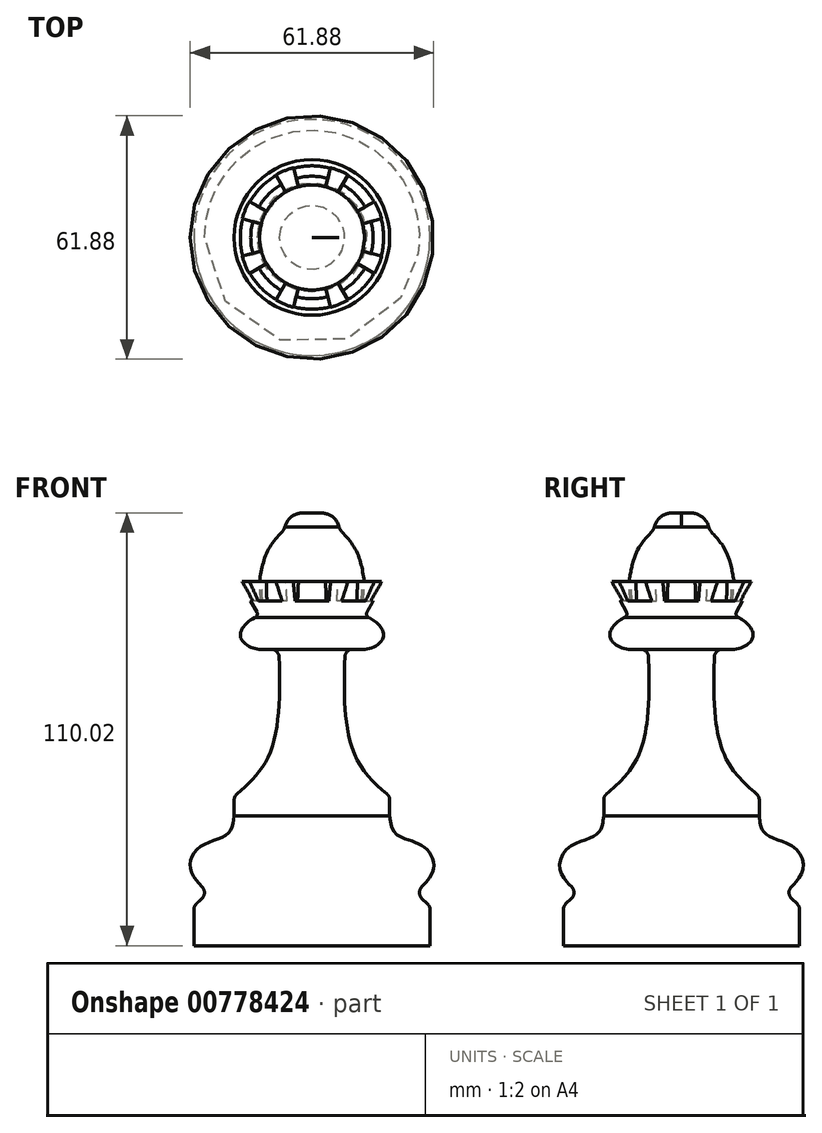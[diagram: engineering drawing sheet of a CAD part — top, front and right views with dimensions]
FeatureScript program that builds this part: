
annotation { "Feature Type Name" : "Feature", "Feature Type Description" : "" }
export const myFeature = defineFeature(function(context is Context, id is Id, definition is map)
    precondition{}
    {
        {
            var Q0;
            Q0=qCreatedBy(makeId("Front.planeOp"),FACE);
            var sketch = newSketch(context, id + "F0", { "sketchPlane" : qUnion([Q0])});
            skLineSegment(sketch, "E0", {"start": v(0, 0) * mm, "end": v(30, 0) * mm});
            skLineSegment(sketch, "E1", {"start": v(30, 0) * mm, "end": v(30, 10) * mm});
            skLineSegment(sketch, "E2", {"start": v(30, 10) * mm, "end": v(26.46, 13.53) * mm});
            skPoint(sketch, "E3.2.internal.snap0", {"position": v(28.23, 11.77) * mm});
            skFitSpline(sketch, "E3", {"points": [v(26.46, 13.53) * mm, v(30.89, 19.7) * mm, v(28.23, 25.27) * mm, v(21.35, 28.45) * mm, v(19.76, 32.96) * mm], "startDerivative": vector(22.56, 21.82) * mm, "endDerivative": vector(-2.53, 23.93) * mm});
            skLineSegment(sketch, "E4", {"start": v(19.76, 32.96) * mm, "end": v(19.76, 37.96) * mm});
            skFitSpline(sketch, "E5", {"points": [v(19.76, 37.96) * mm, v(10.75, 48.85) * mm, v(8.46, 75.35) * mm], "startDerivative": vector(-25.28, 21.61) * mm, "endDerivative": vector(2.63, 51.62) * mm});
            skLineSegment(sketch, "E6", {"start": v(8.46, 75.35) * mm, "end": v(13.46, 75.35) * mm});
            skFitSpline(sketch, "E7", {"points": [v(13.46, 75.35) * mm, v(18.17, 78.53) * mm, v(13.46, 83.83) * mm], "startDerivative": vector(11.88, 0.45) * mm, "endDerivative": vector(-15.94, 5.75) * mm});
            skLineSegment(sketch, "E8", {"start": v(13.46, 83.83) * mm, "end": v(18.34, 92.56) * mm});
            skLineSegment(sketch, "E9", {"start": v(18.34, 92.56) * mm, "end": v(13.34, 92.56) * mm});
            skLineSegment(sketch, "E10", {"start": v(0, 0) * mm, "end": v(0, 110) * mm});
            skFitSpline(sketch, "E11", {"points": [v(13.34, 92.56) * mm, v(11.31, 100.2) * mm, v(7.05, 105.75) * mm], "startDerivative": vector(-2.67, 15.7) * mm, "endDerivative": vector(-9.98, 10.62) * mm});
            skFitSpline(sketch, "E12", {"points": [v(7.05, 105.75) * mm, v(4.34, 109.53) * mm, v(0, 110) * mm], "startDerivative": vector(-2.1, 13) * mm, "endDerivative": vector(-12.92, -0.33) * mm});
            skSolve(sketch);
        }
        {
            var Q0;
            Q0 = qSketchRegion(id + "F0", true);
            var Q1;
            Q1=sQuery(id+"F0.wireOp",EDGE,"E10");
            revolve(context, id + "F1", {"surfaceOperationType" : NewSurfaceOperationType.NEW, "entities" : qUnion([Q0]), "axis" : qUnion([Q1]), "revolveType" : RevolveType.FULL});
        }
        {
            var Q0;
            Q0=makeQuery(id+"F1.opRevolve","SWEPT_FACE",FACE,{"disambiguationData":[OSD([sQuery(id+"F0.wireOp",EDGE,"E9")])]});
            var sketch = newSketch(context, id + "F2", { "sketchPlane" : qUnion([Q0])});
            skArc(sketch, "E13", {"start": v(3.36, 12.53) * mm, "mid": v(0, 12.97) * mm, "end": v(-3.36, 12.53) * mm});
            skArc(sketch, "E14", {"start": v(5.12, 19.11) * mm, "mid": v(0, 19.79) * mm, "end": v(-5.12, 19.11) * mm});
            skLineSegment(sketch, "E15", {"start": v(3.36, 12.53) * mm, "end": v(5.12, 19.11) * mm});
            skLineSegment(sketch, "E16", {"start": v(-3.36, 12.53) * mm, "end": v(-5.12, 19.11) * mm});
            skLineSegment(sketch, "E17.1.0", {"start": v(-6.49, 11.23) * mm, "end": v(-9.9, 17.13) * mm});
            skArc(sketch, "E17.1.1", {"start": v(-9.9, 17.13) * mm, "mid": v(-14, 14) * mm, "end": v(-17.13, 9.9) * mm});
            skLineSegment(sketch, "E17.1.2", {"start": v(-11.23, 6.49) * mm, "end": v(-17.13, 9.9) * mm});
            skArc(sketch, "E17.1.3", {"start": v(-6.49, 11.23) * mm, "mid": v(-9.17, 9.17) * mm, "end": v(-11.23, 6.49) * mm});
            skLineSegment(sketch, "E17.2.0", {"start": v(-12.53, 3.36) * mm, "end": v(-19.11, 5.12) * mm});
            skArc(sketch, "E17.2.1", {"start": v(-19.11, 5.12) * mm, "mid": v(-19.79, 0) * mm, "end": v(-19.11, -5.12) * mm});
            skLineSegment(sketch, "E17.2.2", {"start": v(-12.53, -3.36) * mm, "end": v(-19.11, -5.12) * mm});
            skArc(sketch, "E17.2.3", {"start": v(-12.53, 3.36) * mm, "mid": v(-12.97, 0) * mm, "end": v(-12.53, -3.36) * mm});
            skLineSegment(sketch, "E17.3.0", {"start": v(-11.23, -6.49) * mm, "end": v(-17.13, -9.9) * mm});
            skArc(sketch, "E17.3.1", {"start": v(-17.13, -9.9) * mm, "mid": v(-14, -14) * mm, "end": v(-9.9, -17.13) * mm});
            skLineSegment(sketch, "E17.3.2", {"start": v(-6.49, -11.23) * mm, "end": v(-9.9, -17.13) * mm});
            skArc(sketch, "E17.3.3", {"start": v(-11.23, -6.49) * mm, "mid": v(-9.17, -9.17) * mm, "end": v(-6.49, -11.23) * mm});
            skLineSegment(sketch, "E17.4.0", {"start": v(-3.36, -12.53) * mm, "end": v(-5.12, -19.11) * mm});
            skArc(sketch, "E17.4.1", {"start": v(-5.12, -19.11) * mm, "mid": v(0, -19.79) * mm, "end": v(5.12, -19.11) * mm});
            skLineSegment(sketch, "E17.4.2", {"start": v(3.36, -12.53) * mm, "end": v(5.12, -19.11) * mm});
            skArc(sketch, "E17.4.3", {"start": v(-3.36, -12.53) * mm, "mid": v(0, -12.97) * mm, "end": v(3.36, -12.53) * mm});
            skLineSegment(sketch, "E17.5.0", {"start": v(6.49, -11.23) * mm, "end": v(9.9, -17.13) * mm});
            skArc(sketch, "E17.5.1", {"start": v(9.9, -17.13) * mm, "mid": v(14, -14) * mm, "end": v(17.13, -9.9) * mm});
            skLineSegment(sketch, "E17.5.2", {"start": v(11.23, -6.49) * mm, "end": v(17.13, -9.9) * mm});
            skArc(sketch, "E17.5.3", {"start": v(6.49, -11.23) * mm, "mid": v(9.17, -9.17) * mm, "end": v(11.23, -6.49) * mm});
            skLineSegment(sketch, "E17.6.0", {"start": v(12.53, -3.36) * mm, "end": v(19.11, -5.12) * mm});
            skArc(sketch, "E17.6.1", {"start": v(19.11, -5.12) * mm, "mid": v(19.79, 0) * mm, "end": v(19.11, 5.12) * mm});
            skLineSegment(sketch, "E17.6.2", {"start": v(12.53, 3.36) * mm, "end": v(19.11, 5.12) * mm});
            skArc(sketch, "E17.6.3", {"start": v(12.53, -3.36) * mm, "mid": v(12.97, 0) * mm, "end": v(12.53, 3.36) * mm});
            skLineSegment(sketch, "E17.7.0", {"start": v(11.23, 6.49) * mm, "end": v(17.13, 9.9) * mm});
            skArc(sketch, "E17.7.1", {"start": v(17.13, 9.9) * mm, "mid": v(14, 14) * mm, "end": v(9.9, 17.13) * mm});
            skLineSegment(sketch, "E17.7.2", {"start": v(6.49, 11.23) * mm, "end": v(9.9, 17.13) * mm});
            skArc(sketch, "E17.7.3", {"start": v(11.23, 6.49) * mm, "mid": v(9.17, 9.17) * mm, "end": v(6.49, 11.23) * mm});
            skSolve(sketch);
        }
        {
            var Q0;
            {var subQ0=sQuery(id+"F2.wireOp",EDGE,"E17.2.1");Q0=makeQuery(id+"F2.imprint","IMPRINT",FACE,{"disambiguationData":[TD([[makeQuery(id+"F2.imprint","IMPRINT",EDGE,{"derivedFrom":subQ0}),1.0]])]});}
            var Q1;
            {var subQ0=sQuery(id+"F2.wireOp",EDGE,"E17.2.0");var subQ1=sQuery(id+"F0.wireOp",EDGE,"E9");var subQ2=makeQuery(id+"F1.opRevolve","SWEPT_EDGE",EDGE,{"disambiguationData":[OSD([sQuery(id+"F0.wireOp",EDGE,"E8"),subQ1])]});var subQ3=makeQuery(id+"F2.imprint","INTERSECT",VERTEX,{"derivedFrom":[subQ2,subQ0]});Q1=makeQuery(id+"F2.imprint","IMPRINT",FACE,{"disambiguationData":[TD([[makeQuery(id+"F2.imprint","IMPRINT",EDGE,{"disambiguationData":[TD([[subQ3,1.0]])],"derivedFrom":subQ0}),1.0]])]});}
            var Q2;
            {var subQ0=sQuery(id+"F2.wireOp",EDGE,"E17.1.0");var subQ1=sQuery(id+"F0.wireOp",EDGE,"E9");var subQ2=makeQuery(id+"F1.opRevolve","SWEPT_EDGE",EDGE,{"disambiguationData":[OSD([sQuery(id+"F0.wireOp",EDGE,"E8"),subQ1])]});var subQ3=makeQuery(id+"F2.imprint","INTERSECT",VERTEX,{"derivedFrom":[subQ2,subQ0]});Q2=makeQuery(id+"F2.imprint","IMPRINT",FACE,{"disambiguationData":[TD([[makeQuery(id+"F2.imprint","IMPRINT",EDGE,{"disambiguationData":[TD([[subQ3,1.0]])],"derivedFrom":subQ0}),1.0]])]});}
            var Q3;
            {var subQ0=sQuery(id+"F2.wireOp",EDGE,"E15");var subQ1=sQuery(id+"F0.wireOp",EDGE,"E9");var subQ2=makeQuery(id+"F1.opRevolve","SWEPT_EDGE",EDGE,{"disambiguationData":[OSD([sQuery(id+"F0.wireOp",EDGE,"E8"),subQ1])]});var subQ3=makeQuery(id+"F2.imprint","INTERSECT",VERTEX,{"derivedFrom":[subQ2,subQ0]});Q3=makeQuery(id+"F2.imprint","IMPRINT",FACE,{"disambiguationData":[TD([[makeQuery(id+"F2.imprint","IMPRINT",EDGE,{"disambiguationData":[TD([[subQ3,1.0]])],"derivedFrom":subQ0}),1.0]])]});}
            var Q4;
            {var subQ0=sQuery(id+"F2.wireOp",EDGE,"E17.7.0");var subQ1=sQuery(id+"F0.wireOp",EDGE,"E9");var subQ2=makeQuery(id+"F1.opRevolve","SWEPT_EDGE",EDGE,{"disambiguationData":[OSD([sQuery(id+"F0.wireOp",EDGE,"E8"),subQ1])]});var subQ3=makeQuery(id+"F2.imprint","INTERSECT",VERTEX,{"derivedFrom":[subQ2,subQ0]});Q4=makeQuery(id+"F2.imprint","IMPRINT",FACE,{"disambiguationData":[TD([[makeQuery(id+"F2.imprint","IMPRINT",EDGE,{"disambiguationData":[TD([[subQ3,1.0]])],"derivedFrom":subQ0}),1.0]])]});}
            var Q5;
            {var subQ0=sQuery(id+"F2.wireOp",EDGE,"E17.6.0");var subQ1=sQuery(id+"F0.wireOp",EDGE,"E9");var subQ2=makeQuery(id+"F1.opRevolve","SWEPT_EDGE",EDGE,{"disambiguationData":[OSD([sQuery(id+"F0.wireOp",EDGE,"E8"),subQ1])]});var subQ3=makeQuery(id+"F2.imprint","INTERSECT",VERTEX,{"derivedFrom":[subQ2,subQ0]});Q5=makeQuery(id+"F2.imprint","IMPRINT",FACE,{"disambiguationData":[TD([[makeQuery(id+"F2.imprint","IMPRINT",EDGE,{"disambiguationData":[TD([[subQ3,1.0]])],"derivedFrom":subQ0}),1.0]])]});}
            var Q6;
            {var subQ0=sQuery(id+"F2.wireOp",EDGE,"E17.5.0");var subQ1=sQuery(id+"F0.wireOp",EDGE,"E9");var subQ2=makeQuery(id+"F1.opRevolve","SWEPT_EDGE",EDGE,{"disambiguationData":[OSD([sQuery(id+"F0.wireOp",EDGE,"E8"),subQ1])]});var subQ3=makeQuery(id+"F2.imprint","INTERSECT",VERTEX,{"derivedFrom":[subQ2,subQ0]});Q6=makeQuery(id+"F2.imprint","IMPRINT",FACE,{"disambiguationData":[TD([[makeQuery(id+"F2.imprint","IMPRINT",EDGE,{"disambiguationData":[TD([[subQ3,1.0]])],"derivedFrom":subQ0}),1.0]])]});}
            var Q7;
            {var subQ0=sQuery(id+"F2.wireOp",EDGE,"E17.4.0");var subQ1=sQuery(id+"F0.wireOp",EDGE,"E9");var subQ2=makeQuery(id+"F1.opRevolve","SWEPT_EDGE",EDGE,{"disambiguationData":[OSD([sQuery(id+"F0.wireOp",EDGE,"E8"),subQ1])]});var subQ3=makeQuery(id+"F2.imprint","INTERSECT",VERTEX,{"derivedFrom":[subQ2,subQ0]});Q7=makeQuery(id+"F2.imprint","IMPRINT",FACE,{"disambiguationData":[TD([[makeQuery(id+"F2.imprint","IMPRINT",EDGE,{"disambiguationData":[TD([[subQ3,1.0]])],"derivedFrom":subQ0}),1.0]])]});}
            var Q8;
            {var subQ0=sQuery(id+"F2.wireOp",EDGE,"E17.3.0");var subQ1=sQuery(id+"F0.wireOp",EDGE,"E9");var subQ2=makeQuery(id+"F1.opRevolve","SWEPT_EDGE",EDGE,{"disambiguationData":[OSD([sQuery(id+"F0.wireOp",EDGE,"E8"),subQ1])]});var subQ3=makeQuery(id+"F2.imprint","INTERSECT",VERTEX,{"derivedFrom":[subQ2,subQ0]});Q8=makeQuery(id+"F2.imprint","IMPRINT",FACE,{"disambiguationData":[TD([[makeQuery(id+"F2.imprint","IMPRINT",EDGE,{"disambiguationData":[TD([[subQ3,1.0]])],"derivedFrom":subQ0}),1.0]])]});}
            var Q9;
            Q9=sQuery(id+"F2.wireOp",EDGE,"E17.4.1");
            var Q10;
            Q10=sQuery(id+"F2.wireOp",EDGE,"E17.4.0");
            var Q11;
            Q11=sQuery(id+"F2.wireOp",EDGE,"E17.4.3");
            var Q12;
            Q12=sQuery(id+"F2.wireOp",EDGE,"E17.4.2");
            var Q13;
            Q13=sQuery(id+"F2.wireOp",EDGE,"E17.5.0");
            var Q14;
            Q14=sQuery(id+"F2.wireOp",EDGE,"E17.5.3");
            var Q15;
            Q15=sQuery(id+"F2.wireOp",EDGE,"E17.5.1");
            var Q16;
            Q16=sQuery(id+"F2.wireOp",EDGE,"E17.5.2");
            var Q17;
            Q17=sQuery(id+"F2.wireOp",EDGE,"E17.6.0");
            var Q18;
            Q18=sQuery(id+"F2.wireOp",EDGE,"E17.6.3");
            var Q19;
            Q19=sQuery(id+"F2.wireOp",EDGE,"E17.6.2");
            var Q20;
            Q20=sQuery(id+"F2.wireOp",EDGE,"E17.6.1");
            var Q21;
            Q21=sQuery(id+"F2.wireOp",EDGE,"E17.7.3");
            var Q22;
            Q22=sQuery(id+"F2.wireOp",EDGE,"E17.7.2");
            var Q23;
            Q23=sQuery(id+"F2.wireOp",EDGE,"E17.7.1");
            var Q24;
            Q24=sQuery(id+"F2.wireOp",EDGE,"E17.7.0");
            var Q25;
            Q25=sQuery(id+"F2.wireOp",EDGE,"E15");
            var Q26;
            Q26=sQuery(id+"F2.wireOp",EDGE,"E14");
            var Q27;
            Q27=sQuery(id+"F2.wireOp",EDGE,"E16");
            var Q28;
            Q28=sQuery(id+"F2.wireOp",EDGE,"E13");
            var Q29;
            Q29=sQuery(id+"F2.wireOp",EDGE,"E17.1.3");
            var Q30;
            Q30=sQuery(id+"F2.wireOp",EDGE,"E17.1.0");
            var Q31;
            Q31=sQuery(id+"F2.wireOp",EDGE,"E17.1.1");
            var Q32;
            Q32=sQuery(id+"F2.wireOp",EDGE,"E17.1.2");
            var Q33;
            Q33=sQuery(id+"F2.wireOp",EDGE,"E17.2.0");
            var Q34;
            Q34=sQuery(id+"F2.wireOp",EDGE,"E17.2.1");
            var Q35;
            Q35=sQuery(id+"F2.wireOp",EDGE,"E17.2.2");
            var Q36;
            Q36=sQuery(id+"F2.wireOp",EDGE,"E17.2.3");
            var Q37;
            Q37=sQuery(id+"F2.wireOp",EDGE,"E17.3.0");
            var Q38;
            Q38=sQuery(id+"F2.wireOp",EDGE,"E17.3.3");
            var Q39;
            Q39=sQuery(id+"F2.wireOp",EDGE,"E17.3.2");
            var Q40;
            Q40=sQuery(id+"F2.wireOp",EDGE,"E17.3.1");
            extrude(context, id + "F3", {"entities" : qUnion([Q0, Q1, Q2, Q3, Q4, Q5, Q6, Q7, Q8]), "operationType" : NewBodyOperationType.REMOVE, "surfaceEntities" : qUnion([Q9, Q10, Q11, Q12, Q13, Q14, Q15, Q16, Q17, Q18, Q19, Q20, Q21, Q22, Q23, Q24, Q25, Q26, Q27, Q28, Q29, Q30, Q31, Q32, Q33, Q34, Q35, Q36, Q37, Q38, Q39, Q40]), "oppositeDirection" : true, "depth" : 5 * mm, "offsetDistance" : 25 * mm, "hasDraft" : true, "draftAngle" : 3 * degree});
        }
        {
            var Q0;
            Q0=makeQuery(id+"F1.opRevolve","SWEPT_EDGE",EDGE,{"disambiguationData":[OSD([sQuery(id+"F0.wireOp",EDGE,"E11"),sQuery(id+"F0.wireOp",EDGE,"E12")])]});
            fillet(context, id + "F4", {"entities" : qUnion([Q0]), "radius" : 3 * mm, "tangentPropagation" : true, "allowEdgeOverflow" : false});
        }
        {
            var Q0;
            Q0=makeQuery(id+"F1.opRevolve","SWEPT_EDGE",EDGE,{"disambiguationData":[OSD([sQuery(id+"F0.wireOp",EDGE,"E7"),sQuery(id+"F0.wireOp",EDGE,"E8")])]});
            fillet(context, id + "F5", {"entities" : qUnion([Q0]), "radius" : 1 * mm, "tangentPropagation" : true, "allowEdgeOverflow" : false});
        }
        {
            var Q0;
            Q0=makeQuery(id+"F1.opRevolve","SWEPT_EDGE",EDGE,{"disambiguationData":[OSD([sQuery(id+"F0.wireOp",EDGE,"E5"),sQuery(id+"F0.wireOp",EDGE,"E6")])]});
            fillet(context, id + "F6", {"entities" : qUnion([Q0]), "radius" : 2 * mm, "tangentPropagation" : true, "allowEdgeOverflow" : false});
        }
        {
            var Q0;
            Q0=makeQuery(id+"F1.opRevolve","SWEPT_EDGE",EDGE,{"disambiguationData":[OSD([sQuery(id+"F0.wireOp",EDGE,"E2"),sQuery(id+"F0.wireOp",EDGE,"E3")])]});
            fillet(context, id + "F7", {"entities" : qUnion([Q0]), "radius" : 2 * mm, "tangentPropagation" : true, "allowEdgeOverflow" : false});
        }
        {
            var Q0;
            Q0=makeQuery(id+"F1.opRevolve","SWEPT_EDGE",EDGE,{"disambiguationData":[OSD([sQuery(id+"F0.wireOp",EDGE,"E1"),sQuery(id+"F0.wireOp",EDGE,"E2")])]});
            fillet(context, id + "F8", {"entities" : qUnion([Q0]), "radius" : 2 * mm, "tangentPropagation" : true, "allowEdgeOverflow" : false});
        }
        {
            var Q0;
            Q0=makeQuery(id+"F1.opRevolve","SWEPT_EDGE",EDGE,{"disambiguationData":[OSD([sQuery(id+"F0.wireOp",EDGE,"E4"),sQuery(id+"F0.wireOp",EDGE,"E5")])]});
            fillet(context, id + "F9", {"entities" : qUnion([Q0]), "radius" : 2 * mm, "tangentPropagation" : true, "allowEdgeOverflow" : false});
        }
    });
